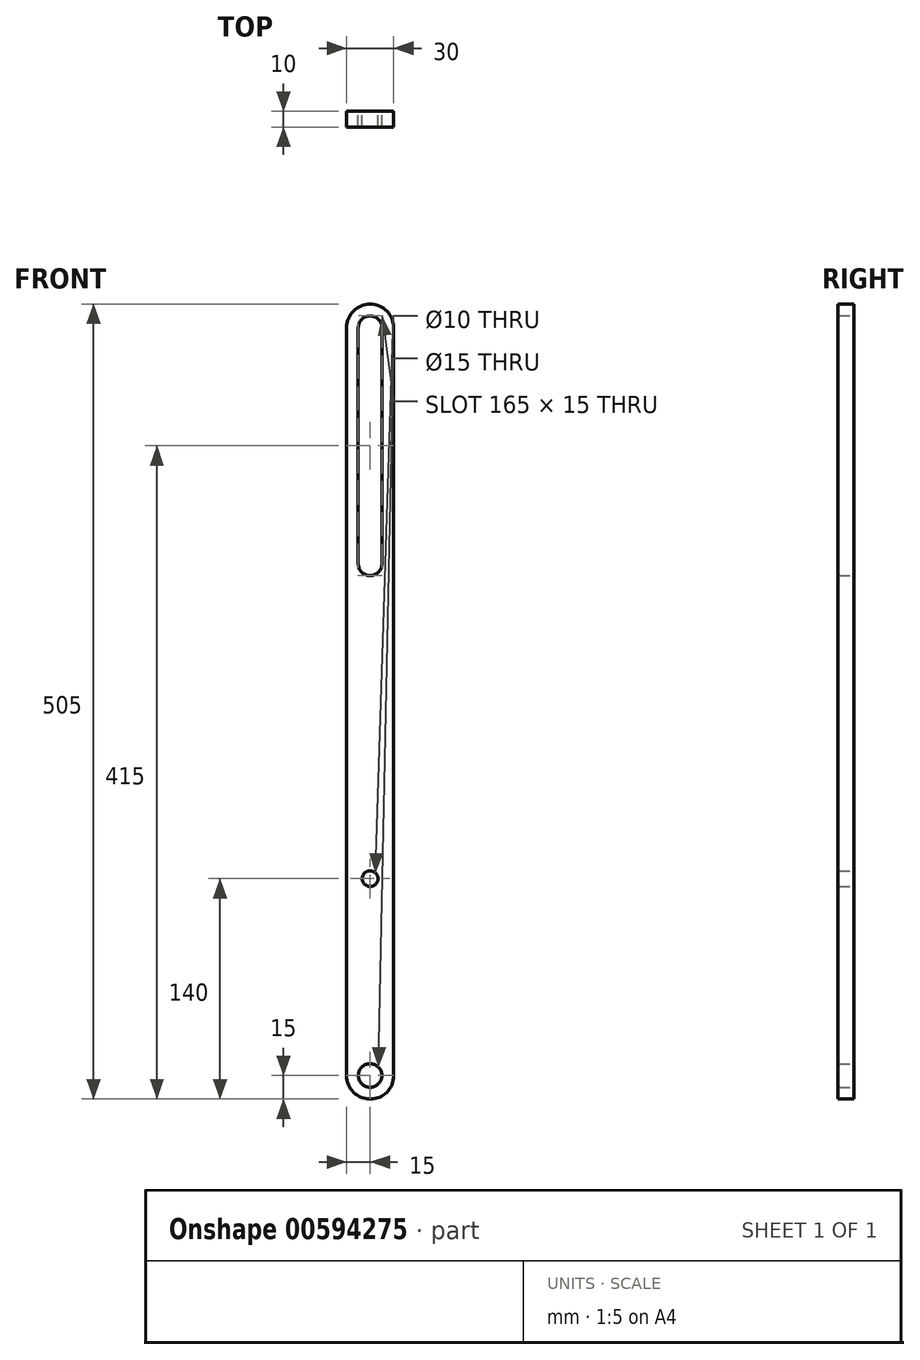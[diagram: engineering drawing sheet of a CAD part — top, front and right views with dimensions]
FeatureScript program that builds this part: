
annotation { "Feature Type Name" : "Feature", "Feature Type Description" : "" }
export const myFeature = defineFeature(function(context is Context, id is Id, definition is map)
    precondition{}
    {
        {
            var Q0;
            Q0=qCreatedBy(makeId("Front.planeOp"),FACE);
            var sketch = newSketch(context, id + "F0", { "sketchPlane" : qUnion([Q0])});
            skLineSegment(sketch, "E0", {"start": v(0, 0) * mm, "end": v(0, 475) * mm, "construction": true});
            skArc(sketch, "E1", {"start": v(7.5, 475) * mm, "mid": v(0, 482.5) * mm, "end": v(-7.5, 475) * mm});
            skCircle(sketch, "E2", {"center": v(0, 0) * mm, "radius": 7.5 * mm});
            skArc(sketch, "E3", {"start": v(-15, 0) * mm, "mid": v(0, -15) * mm, "end": v(15, 0) * mm});
            skArc(sketch, "E4", {"start": v(15, 475) * mm, "mid": v(0, 490) * mm, "end": v(-15, 475) * mm});
            skLineSegment(sketch, "E5", {"start": v(0, 475) * mm, "end": v(-15, 475) * mm, "construction": true});
            skLineSegment(sketch, "E6", {"start": v(0, 0) * mm, "end": v(-15, 0) * mm, "construction": true});
            skLineSegment(sketch, "E7", {"start": v(-15, 0) * mm, "end": v(-15, 475) * mm});
            skLineSegment(sketch, "E8.MirrorCS", {"start": v(15, 0) * mm, "end": v(15, 475) * mm});
            skCircle(sketch, "E9", {"center": v(0, 125) * mm, "radius": 5 * mm});
            skArc(sketch, "E10", {"start": v(-7.5, 325) * mm, "mid": v(0, 317.5) * mm, "end": v(7.5, 325) * mm});
            skLineSegment(sketch, "E11.MirrorCS", {"start": v(7.5, 475) * mm, "end": v(7.5, 325) * mm});
            skLineSegment(sketch, "E12", {"start": v(-7.5, 475) * mm, "end": v(-7.5, 325) * mm});
            skSolve(sketch);
        }
        {
            var Q0;
            Q0=makeQuery(id+"F0.imprint","IMPRINT",FACE,{"disambiguationData":[TD([[makeQuery(id+"F0.imprint","IMPRINT",EDGE,{"derivedFrom":sQuery(id+"F0.wireOp",EDGE,"E1")}),-1.0]])]});
            extrude(context, id + "F1", {"entities" : qUnion([Q0]), "depth" : 10 * mm, "offsetDistance" : 25 * mm});
        }
    });
